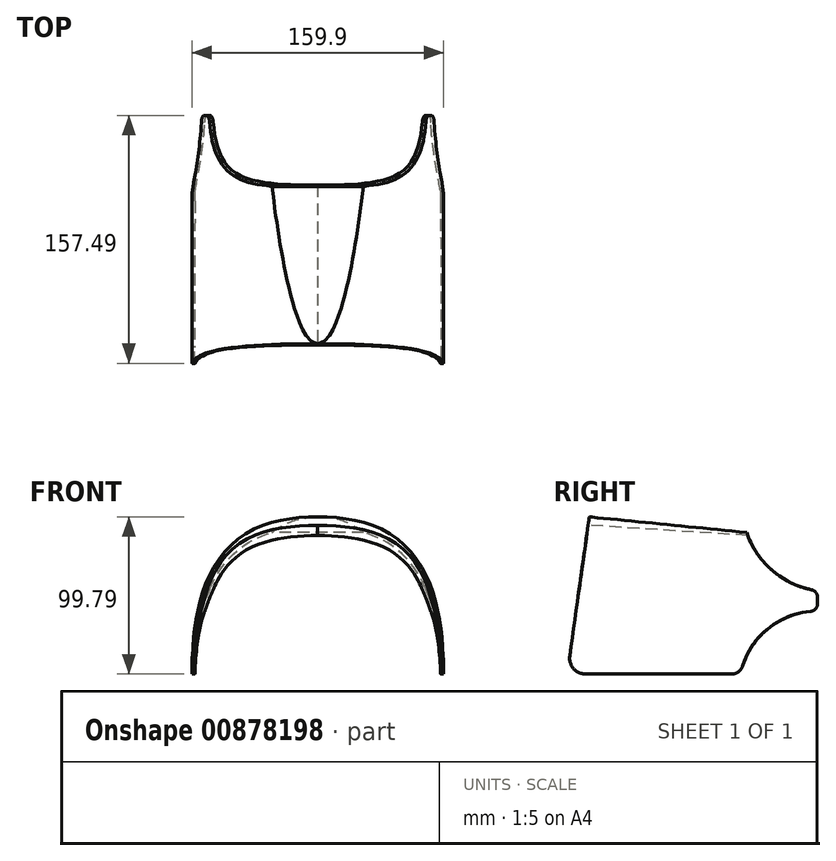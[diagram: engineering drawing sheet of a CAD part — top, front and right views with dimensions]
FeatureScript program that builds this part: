
annotation { "Feature Type Name" : "Feature", "Feature Type Description" : "" }
export const myFeature = defineFeature(function(context is Context, id is Id, definition is map)
    precondition{}
    {
        {
            var Q0;
            Q0=qCreatedBy(makeId("Right.planeOp"),FACE);
            var sketch = newSketch(context, id + "F0", { "sketchPlane" : qUnion([Q0])});
            skLineSegment(sketch, "E0.top", {"start": v(-40.12, -51.54) * mm, "end": v(69.88, -51.54) * mm});
            skLineSegment(sketch, "E0.right", {"start": v(118.87, 1.36) * mm, "end": v(118.87, -11.54) * mm});
            skArc(sketch, "E1", {"start": v(118.87, -11.54) * mm, "mid": v(87.25, -22.81) * mm, "end": v(69.88, -51.54) * mm});
            skLineSegment(sketch, "E2", {"start": v(138.17, -11.54) * mm, "end": v(-128.74, -11.54) * mm, "construction": true});
            skArc(sketch, "E3", {"start": v(73.87, 38.36) * mm, "mid": v(91.07, 13.41) * mm, "end": v(118.87, 1.36) * mm});
            skLineSegment(sketch, "E4", {"start": v(-26.13, 69.35) * mm, "end": v(-26.13, -71.85) * mm, "construction": true});
            skLineSegment(sketch, "E5", {"start": v(-26.13, 48.25) * mm, "end": v(-40.12, -51.54) * mm});
            skLineSegment(sketch, "E6", {"start": v(-26.13, 48.25) * mm, "end": v(73.87, 38.36) * mm});
            skLineSegment(sketch, "E7", {"start": v(73.87, 71.96) * mm, "end": v(73.87, 6.4) * mm, "construction": true});
            skSolve(sketch);
        }
        {
            var Q0;
            Q0=makeQuery(id+"F0.imprint","IMPRINT",FACE,{"disambiguationData":[TD([[makeQuery(id+"F0.imprint","IMPRINT",EDGE,{"derivedFrom":sQuery(id+"F0.wireOp",EDGE,"E0.bottom")}),-1.0]])]});
            var Q1;
            Q1=makeQuery(id+"F0.imprint","IMPRINT",FACE,{"disambiguationData":[TD([[makeQuery(id+"F0.imprint","IMPRINT",EDGE,{"derivedFrom":sQuery(id+"F0.wireOp",EDGE,"E0.top")}),1.0]])]});
            extrude(context, id + "F1", {"entities" : qUnion([Q0, Q1]), "endBound" : BoundingType.SYMMETRIC, "depth" : 160 * mm, "offsetDistance" : 25 * mm});
        }
        {
            var Q0;
            Q0=qCreatedBy(makeId("Front.planeOp"),FACE);
            var Q1;
            Q1=makeQuery(id+"F1.opExtrude","SWEPT_EDGE",EDGE,{"disambiguationData":[OSD([sQuery(id+"F0.wireOp",EDGE,"E5"),sQuery(id+"F0.wireOp",EDGE,"E6")])]});
            cPlane(context, id + "F2", {"entities" : qUnion([Q0, Q1]), "cplaneType" : CPlaneType.LINE_ANGLE, "offset" : 25 * mm, "angle" : 3.65 * degree, "width" : 150 * mm, "height" : 150 * mm});
        }
        {
            var Q0;
            Q0=qCreatedBy(id+"F2.planeOp",FACE);
            var sketch = newSketch(context, id + "F3", { "sketchPlane" : qUnion([Q0])});
            skLineSegment(sketch, "E8", {"start": v(0, 102.22) * mm, "end": v(0, -79.39) * mm, "construction": true});
            skLineSegment(sketch, "E9", {"start": v(146.17, 46.49) * mm, "end": v(-146.43, 46.49) * mm, "construction": true});
            skFitSpline(sketch, "E10", {"points": [v(0, 46.49) * mm, v(57.65, 25.74) * mm, v(73.2, -2.02) * mm, v(80, -59.97) * mm], "startDerivative": vector(255.44, 0) * mm, "endDerivative": vector(0, -226.5) * mm});
            skLineSegment(sketch, "E11", {"start": v(80, 56.96) * mm, "end": v(80, -84.78) * mm, "construction": true});
            skFitSpline(sketch, "E12", {"points": [v(-1.7, 41.17) * mm, v(56, 24.21) * mm, v(71.49, -3.53) * mm, v(78.3, -61.5) * mm], "startDerivative": vector(255.46, 0) * mm, "endDerivative": vector(0, -226.5) * mm});
            skFitSpline(sketch, "E13.MirrorCS", {"points": [v(0, 46.49) * mm, v(-57.65, 25.74) * mm, v(-73.2, -2.02) * mm, v(-80, -59.97) * mm], "startDerivative": vector(-255.44, 0) * mm, "endDerivative": vector(0, -226.5) * mm});
            skFitSpline(sketch, "E14.MirrorCS", {"points": [v(1.7, 41.17) * mm, v(-56, 24.21) * mm, v(-71.49, -3.53) * mm, v(-78.3, -61.5) * mm], "startDerivative": vector(-255.46, 0) * mm, "endDerivative": vector(0, -226.5) * mm});
            skLineSegment(sketch, "E15", {"start": v(80, -59.97) * mm, "end": v(133.34, -11.85) * mm});
            skLineSegment(sketch, "E16", {"start": v(133.34, -11.85) * mm, "end": v(48.44, 102.7) * mm});
            skLineSegment(sketch, "E17", {"start": v(48.44, 102.7) * mm, "end": v(-66, 102.7) * mm});
            skLineSegment(sketch, "E18", {"start": v(-66, 102.7) * mm, "end": v(-136.93, -18.29) * mm});
            skLineSegment(sketch, "E19", {"start": v(-136.93, -18.29) * mm, "end": v(-80, -59.97) * mm});
            skLineSegment(sketch, "E20", {"start": v(78.3, -60) * mm, "end": v(-78.3, -60) * mm});
            skSolve(sketch);
        }
        {
            var Q0;
            Q0=makeQuery(id+"F3.imprint","IMPRINT",FACE,{"disambiguationData":[TD([[makeQuery(id+"F3.imprint","IMPRINT",EDGE,{"derivedFrom":sQuery(id+"F3.wireOp",EDGE,"E10")}),1.0]])]});
            extrude(context, id + "F4", {"entities" : qUnion([Q0]), "operationType" : NewBodyOperationType.REMOVE, "endBound" : BoundingType.SYMMETRIC, "depth" : 608 * mm, "offsetDistance" : 25 * mm});
        }
        {
            var Q0;
            Q0=makeQuery(id+"F3.imprint","IMPRINT",FACE,{"disambiguationData":[TD([[makeQuery(id+"F3.imprint","IMPRINT",EDGE,{"derivedFrom":sQuery(id+"F3.wireOp",EDGE,"E12")}),-1.0]])]});
            extrude(context, id + "F5", {"entities" : qUnion([Q0]), "operationType" : NewBodyOperationType.REMOVE, "endBound" : BoundingType.SYMMETRIC, "depth" : 588 * mm, "offsetDistance" : 25 * mm});
        }
        {
            var Q0;
            {var subQ0=sQuery(id+"F0.wireOp",EDGE,"E0.top");var subQ1=sQuery(id+"F0.wireOp",EDGE,"E5");Q0=makeQuery(id+"F5.boolean.opBoolean","SPLIT",EDGE,{"disambiguationData":[TD([makeQuery(id+"F4.boolean.opBoolean","COPY",FACE,{"derivedFrom":makeQuery(id+"F4.opExtrude","SWEPT_FACE",FACE,{"disambiguationData":[OSD([sQuery(id+"F3.wireOp",EDGE,"E13.MirrorCS")])]})})])],"derivedFrom":makeQuery(id+"F1.opExtrude","SWEPT_EDGE",EDGE,{"disambiguationData":[OSD([subQ0,subQ1])]})});}
            var Q1;
            {var subQ0=sQuery(id+"F0.wireOp",EDGE,"E0.top");var subQ1=sQuery(id+"F0.wireOp",EDGE,"E5");Q1=makeQuery(id+"F5.boolean.opBoolean","SPLIT",EDGE,{"disambiguationData":[TD([makeQuery(id+"F4.boolean.opBoolean","COPY",FACE,{"derivedFrom":makeQuery(id+"F4.opExtrude","SWEPT_FACE",FACE,{"disambiguationData":[OSD([sQuery(id+"F3.wireOp",EDGE,"E10")])]})})])],"derivedFrom":makeQuery(id+"F1.opExtrude","SWEPT_EDGE",EDGE,{"disambiguationData":[OSD([subQ0,subQ1])]})});}
            fillet(context, id + "F6", {"entities" : qUnion([Q0, Q1]), "radius" : 10 * mm, "tangentPropagation" : true, "allowEdgeOverflow" : false});
        }
        {
            var Q0;
            {var subQ0=sQuery(id+"F0.wireOp",EDGE,"E0.top");var subQ1=sQuery(id+"F0.wireOp",EDGE,"E1");Q0=makeQuery(id+"F5.boolean.opBoolean","SPLIT",EDGE,{"disambiguationData":[TD([makeQuery(id+"F4.boolean.opBoolean","COPY",FACE,{"derivedFrom":makeQuery(id+"F4.opExtrude","SWEPT_FACE",FACE,{"disambiguationData":[OSD([sQuery(id+"F3.wireOp",EDGE,"E10")])]})})])],"derivedFrom":makeQuery(id+"F1.opExtrude","SWEPT_EDGE",EDGE,{"disambiguationData":[OSD([subQ0,subQ1])]})});}
            var Q1;
            {var subQ0=sQuery(id+"F0.wireOp",EDGE,"E0.top");var subQ1=sQuery(id+"F0.wireOp",EDGE,"E1");Q1=makeQuery(id+"F5.boolean.opBoolean","SPLIT",EDGE,{"disambiguationData":[TD([makeQuery(id+"F4.boolean.opBoolean","COPY",FACE,{"derivedFrom":makeQuery(id+"F4.opExtrude","SWEPT_FACE",FACE,{"disambiguationData":[OSD([sQuery(id+"F3.wireOp",EDGE,"E13.MirrorCS")])]})})])],"derivedFrom":makeQuery(id+"F1.opExtrude","SWEPT_EDGE",EDGE,{"disambiguationData":[OSD([subQ0,subQ1])]})});}
            fillet(context, id + "F7", {"entities" : qUnion([Q0, Q1]), "radius" : 7 * mm, "tangentPropagation" : true, "allowEdgeOverflow" : false});
        }
        {
            var Q0;
            {var subQ0=sQuery(id+"F0.wireOp",EDGE,"E0.right");var subQ1=sQuery(id+"F0.wireOp",EDGE,"E3");Q0=makeQuery(id+"F5.boolean.opBoolean","SPLIT",EDGE,{"disambiguationData":[TD([makeQuery(id+"F4.boolean.opBoolean","COPY",FACE,{"derivedFrom":makeQuery(id+"F4.opExtrude","SWEPT_FACE",FACE,{"disambiguationData":[OSD([sQuery(id+"F3.wireOp",EDGE,"E13.MirrorCS")])]})})])],"derivedFrom":makeQuery(id+"F1.opExtrude","SWEPT_EDGE",EDGE,{"disambiguationData":[OSD([subQ0,subQ1])]})});}
            var Q1;
            {var subQ0=sQuery(id+"F0.wireOp",EDGE,"E0.right");var subQ1=sQuery(id+"F0.wireOp",EDGE,"E1");Q1=makeQuery(id+"F5.boolean.opBoolean","SPLIT",EDGE,{"disambiguationData":[TD([makeQuery(id+"F4.boolean.opBoolean","COPY",FACE,{"derivedFrom":makeQuery(id+"F4.opExtrude","SWEPT_FACE",FACE,{"disambiguationData":[OSD([sQuery(id+"F3.wireOp",EDGE,"E13.MirrorCS")])]})})])],"derivedFrom":makeQuery(id+"F1.opExtrude","SWEPT_EDGE",EDGE,{"disambiguationData":[OSD([subQ0,subQ1])]})});}
            var Q2;
            {var subQ0=sQuery(id+"F0.wireOp",EDGE,"E0.right");var subQ1=sQuery(id+"F0.wireOp",EDGE,"E3");Q2=makeQuery(id+"F5.boolean.opBoolean","SPLIT",EDGE,{"disambiguationData":[TD([makeQuery(id+"F4.boolean.opBoolean","COPY",FACE,{"derivedFrom":makeQuery(id+"F4.opExtrude","SWEPT_FACE",FACE,{"disambiguationData":[OSD([sQuery(id+"F3.wireOp",EDGE,"E10")])]})})])],"derivedFrom":makeQuery(id+"F1.opExtrude","SWEPT_EDGE",EDGE,{"disambiguationData":[OSD([subQ0,subQ1])]})});}
            var Q3;
            {var subQ0=sQuery(id+"F0.wireOp",EDGE,"E0.right");var subQ1=sQuery(id+"F0.wireOp",EDGE,"E1");Q3=makeQuery(id+"F5.boolean.opBoolean","SPLIT",EDGE,{"disambiguationData":[TD([makeQuery(id+"F4.boolean.opBoolean","COPY",FACE,{"derivedFrom":makeQuery(id+"F4.opExtrude","SWEPT_FACE",FACE,{"disambiguationData":[OSD([sQuery(id+"F3.wireOp",EDGE,"E10")])]})})])],"derivedFrom":makeQuery(id+"F1.opExtrude","SWEPT_EDGE",EDGE,{"disambiguationData":[OSD([subQ0,subQ1])]})});}
            fillet(context, id + "F8", {"entities" : qUnion([Q0, Q1, Q2, Q3]), "radius" : 5 * mm, "tangentPropagation" : true, "allowEdgeOverflow" : false});
        }
    });
